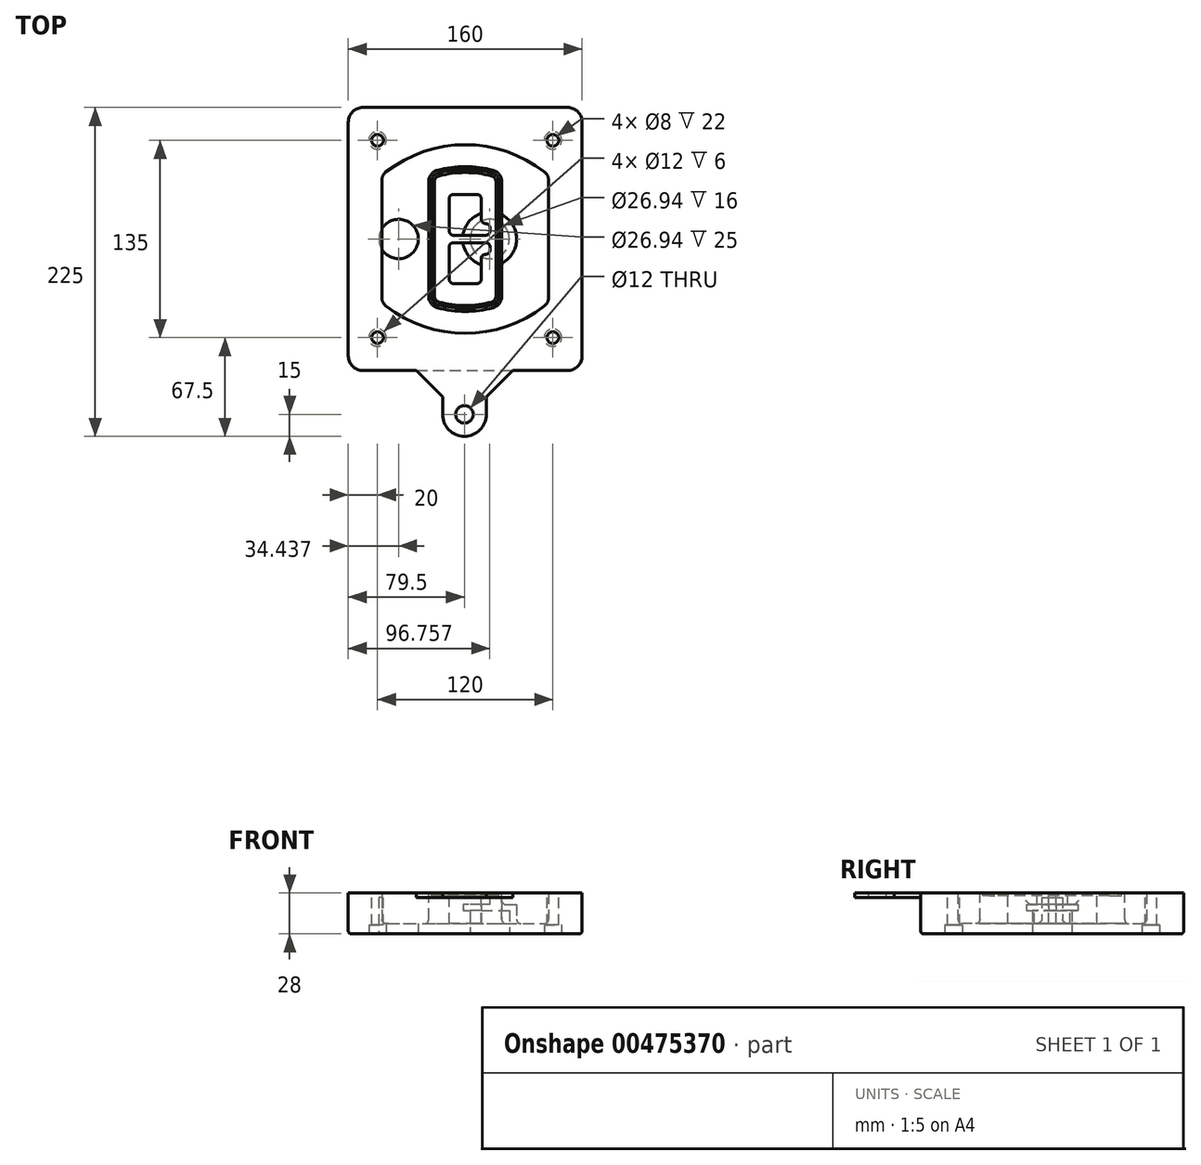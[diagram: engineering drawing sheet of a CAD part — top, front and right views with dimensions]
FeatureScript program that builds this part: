
annotation { "Feature Type Name" : "Feature", "Feature Type Description" : "" }
export const myFeature = defineFeature(function(context is Context, id is Id, definition is map)
    precondition{}
    {
        {
            var Q0;
            Q0=qCreatedBy(makeId("Top.planeOp"),FACE);
            var sketch = newSketch(context, id + "F0", { "sketchPlane" : qUnion([Q0])});
            skPoint(sketch, "E0.rect.middle", {"position": v(0, 0) * mm});
            skLineSegment(sketch, "E1.bottom", {"start": v(-70, -90) * mm, "end": v(70, -90) * mm});
            skLineSegment(sketch, "E1.top", {"start": v(-70, 90) * mm, "end": v(70, 90) * mm});
            skLineSegment(sketch, "E1.left", {"start": v(-80, -80) * mm, "end": v(-80, 80) * mm});
            skLineSegment(sketch, "E1.right", {"start": v(80, -80) * mm, "end": v(80, 80) * mm});
            skLineSegment(sketch, "E2", {"start": v(-80, 90) * mm, "end": v(80, -90) * mm, "construction": true});
            skLineSegment(sketch, "E3", {"start": v(80, 90) * mm, "end": v(-80, -90) * mm, "construction": true});
            skCircle(sketch, "E4", {"center": v(-60, 67.5) * mm, "radius": 4 * mm});
            skCircle(sketch, "E5", {"center": v(60, 67.5) * mm, "radius": 4 * mm});
            skCircle(sketch, "E6", {"center": v(60, -67.5) * mm, "radius": 4 * mm});
            skCircle(sketch, "E7", {"center": v(-60, -67.5) * mm, "radius": 4 * mm});
            skLineSegment(sketch, "E8", {"start": v(-60, 67.5) * mm, "end": v(60, 67.5) * mm, "construction": true});
            skLineSegment(sketch, "E9", {"start": v(60, 67.5) * mm, "end": v(60, -67.5) * mm, "construction": true});
            skLineSegment(sketch, "E10", {"start": v(60, -67.5) * mm, "end": v(-60, -67.5) * mm, "construction": true});
            skLineSegment(sketch, "E11", {"start": v(-60, -67.5) * mm, "end": v(-60, 67.5) * mm, "construction": true});
            skLineSegment(sketch, "E12", {"start": v(-60, 40.3) * mm, "end": v(-60, -40.3) * mm});
            skLineSegment(sketch, "E13", {"start": v(60, 40.3) * mm, "end": v(60, -40.3) * mm});
            skArc(sketch, "E14", {"start": v(56.15, 48.18) * mm, "mid": v(0, 67.5) * mm, "end": v(-56.15, 48.18) * mm});
            skArc(sketch, "E15", {"start": v(-56.15, -48.18) * mm, "mid": v(0, -67.5) * mm, "end": v(56.15, -48.18) * mm});
            skLineSegment(sketch, "E16", {"start": v(-60, 0) * mm, "end": v(60, 0) * mm, "construction": true});
            skPoint(sketch, "E17.visualSharp", {"position": v(-60, -45) * mm});
            skArc(sketch, "E17.filletArc", {"start": v(-60, -40.3) * mm, "mid": v(-58.99, -44.68) * mm, "end": v(-56.15, -48.18) * mm});
            skPoint(sketch, "E18.visualSharp", {"position": v(-60, 45) * mm});
            skArc(sketch, "E18.filletArc", {"start": v(-56.15, 48.18) * mm, "mid": v(-58.99, 44.68) * mm, "end": v(-60, 40.3) * mm});
            skPoint(sketch, "E19.visualSharp", {"position": v(60, 45) * mm});
            skArc(sketch, "E19.filletArc", {"start": v(60, 40.3) * mm, "mid": v(58.99, 44.68) * mm, "end": v(56.15, 48.18) * mm});
            skPoint(sketch, "E20.visualSharp", {"position": v(60, -45) * mm});
            skArc(sketch, "E20.filletArc", {"start": v(56.15, -48.18) * mm, "mid": v(58.99, -44.68) * mm, "end": v(60, -40.3) * mm});
            skPoint(sketch, "E21.visualSharp", {"position": v(-80, 90) * mm});
            skArc(sketch, "E21.filletArc", {"start": v(-70, 90) * mm, "mid": v(-77.07, 87.07) * mm, "end": v(-80, 80) * mm});
            skPoint(sketch, "E22.visualSharp", {"position": v(80, 90) * mm});
            skArc(sketch, "E22.filletArc", {"start": v(80, 80) * mm, "mid": v(77.07, 87.07) * mm, "end": v(70, 90) * mm});
            skPoint(sketch, "E23.visualSharp", {"position": v(80, -90) * mm});
            skArc(sketch, "E23.filletArc", {"start": v(70, -90) * mm, "mid": v(77.07, -87.07) * mm, "end": v(80, -80) * mm});
            skPoint(sketch, "E24.visualSharp", {"position": v(-80, -90) * mm});
            skArc(sketch, "E24.filletArc", {"start": v(-80, -80) * mm, "mid": v(-77.07, -87.07) * mm, "end": v(-70, -90) * mm});
            skArc(sketch, "E25.0", {"start": v(57, 40.3) * mm, "mid": v(56.3, 43.36) * mm, "end": v(54.3, 45.81) * mm});
            skLineSegment(sketch, "E25.1", {"start": v(57, 40.3) * mm, "end": v(57, -40.3) * mm});
            skArc(sketch, "E25.2", {"start": v(54.3, -45.81) * mm, "mid": v(56.3, -43.36) * mm, "end": v(57, -40.3) * mm});
            skArc(sketch, "E25.3", {"start": v(-54.3, -45.81) * mm, "mid": v(0, -64.5) * mm, "end": v(54.3, -45.81) * mm});
            skArc(sketch, "E25.4", {"start": v(-57, -40.3) * mm, "mid": v(-56.3, -43.36) * mm, "end": v(-54.3, -45.81) * mm});
            skArc(sketch, "E25.5", {"start": v(54.3, 45.81) * mm, "mid": v(0, 64.5) * mm, "end": v(-54.3, 45.81) * mm});
            skLineSegment(sketch, "E25.6", {"start": v(-57, 40.3) * mm, "end": v(-57, -40.3) * mm});
            skArc(sketch, "E25.7", {"start": v(-54.3, 45.81) * mm, "mid": v(-56.3, 43.36) * mm, "end": v(-57, 40.3) * mm});
            skArc(sketch, "E26.0", {"start": v(-58.62, 51.33) * mm, "mid": v(-62.58, 46.43) * mm, "end": v(-64, 40.3) * mm});
            skArc(sketch, "E26.1", {"start": v(58.62, 51.33) * mm, "mid": v(0, 71.5) * mm, "end": v(-58.62, 51.33) * mm});
            skArc(sketch, "E26.2", {"start": v(64, 40.3) * mm, "mid": v(62.58, 46.43) * mm, "end": v(58.62, 51.33) * mm});
            skLineSegment(sketch, "E26.3", {"start": v(64, 40.3) * mm, "end": v(64, -40.3) * mm});
            skArc(sketch, "E26.4", {"start": v(58.62, -51.33) * mm, "mid": v(62.58, -46.43) * mm, "end": v(64, -40.3) * mm});
            skLineSegment(sketch, "E26.5", {"start": v(-64, 40.3) * mm, "end": v(-64, -40.3) * mm});
            skArc(sketch, "E26.6", {"start": v(-58.62, -51.33) * mm, "mid": v(0, -71.5) * mm, "end": v(58.62, -51.33) * mm});
            skArc(sketch, "E26.7", {"start": v(-64, -40.3) * mm, "mid": v(-62.58, -46.43) * mm, "end": v(-58.62, -51.33) * mm});
            skSolve(sketch);
        }
        {
            var Q0;
            Q0=makeQuery(id+"F0.imprint","IMPRINT",FACE,{"disambiguationData":[TD([[makeQuery(id+"F0.imprint","IMPRINT",EDGE,{"derivedFrom":sQuery(id+"F0.wireOp",EDGE,"E1.bottom")}),1.0]])]});
            var Q1;
            Q1=makeQuery(id+"F0.imprint","IMPRINT",FACE,{"disambiguationData":[TD([[makeQuery(id+"F0.imprint","IMPRINT",EDGE,{"derivedFrom":sQuery(id+"F0.wireOp",EDGE,"E12")}),1.0]])]});
            var Q2;
            Q2=makeQuery(id+"F0.imprint","IMPRINT",FACE,{"disambiguationData":[TD([[makeQuery(id+"F0.imprint","IMPRINT",EDGE,{"derivedFrom":sQuery(id+"F0.wireOp",EDGE,"E25.0")}),1.0]])]});
            var Q3;
            Q3=makeQuery(id+"F0.imprint","IMPRINT",FACE,{"disambiguationData":[TD([[makeQuery(id+"F0.imprint","IMPRINT",EDGE,{"derivedFrom":sQuery(id+"F0.wireOp",EDGE,"E12")}),-1.0]])]});
            extrude(context, id + "F1", {"entities" : qUnion([Q0, Q1, Q2, Q3]), "oppositeDirection" : true, "depth" : 25 * mm});
        }
        {
            var Q0;
            Q0=makeQuery(id+"F0.imprint","IMPRINT",FACE,{"disambiguationData":[TD([[makeQuery(id+"F0.imprint","IMPRINT",EDGE,{"derivedFrom":sQuery(id+"F0.wireOp",EDGE,"E12")}),1.0]])]});
            extrude(context, id + "F2", {"entities" : qUnion([Q0]), "operationType" : NewBodyOperationType.ADD, "depth" : 3 * mm});
        }
        {
            var Q0;
            Q0=makeQuery(id+"F0.imprint","IMPRINT",FACE,{"disambiguationData":[TD([[makeQuery(id+"F0.imprint","IMPRINT",EDGE,{"derivedFrom":sQuery(id+"F0.wireOp",EDGE,"E25.0")}),1.0]])]});
            extrude(context, id + "F3", {"entities" : qUnion([Q0]), "operationType" : NewBodyOperationType.REMOVE, "oppositeDirection" : true, "depth" : 18 * mm});
        }
        {
            var Q0;
            Q0=makeQuery(id+"F2.opExtrude","CAP_FACE",FACE,{"disambiguationData":[OSD([sQuery(id+"F0.wireOp",EDGE,"E12"),sQuery(id+"F0.wireOp",EDGE,"E13"),sQuery(id+"F0.wireOp",EDGE,"E14"),sQuery(id+"F0.wireOp",EDGE,"E15"),sQuery(id+"F0.wireOp",EDGE,"E17.filletArc"),sQuery(id+"F0.wireOp",EDGE,"E18.filletArc"),sQuery(id+"F0.wireOp",EDGE,"E19.filletArc"),sQuery(id+"F0.wireOp",EDGE,"E20.filletArc"),sQuery(id+"F0.wireOp",EDGE,"E25.0"),sQuery(id+"F0.wireOp",EDGE,"E25.1"),sQuery(id+"F0.wireOp",EDGE,"E25.2"),sQuery(id+"F0.wireOp",EDGE,"E25.3"),sQuery(id+"F0.wireOp",EDGE,"E25.4"),sQuery(id+"F0.wireOp",EDGE,"E25.5"),sQuery(id+"F0.wireOp",EDGE,"E25.6"),sQuery(id+"F0.wireOp",EDGE,"E25.7")])],"isStart":false});
            var sketch = newSketch(context, id + "F4", { "sketchPlane" : qUnion([Q0])});
            skArc(sketch, "E27.0", {"start": v(-19.08, -46.97) * mm, "mid": v(0, -49.5) * mm, "end": v(19.08, -46.97) * mm});
            skArc(sketch, "E28.0", {"start": v(19.08, 46.97) * mm, "mid": v(0, 49.5) * mm, "end": v(-19.08, 46.97) * mm});
            skLineSegment(sketch, "E29", {"start": v(-25, 39.25) * mm, "end": v(-25, -39.25) * mm});
            skLineSegment(sketch, "E30", {"start": v(25, 39.25) * mm, "end": v(25, -39.25) * mm});
            skLineSegment(sketch, "E31", {"start": v(-25, 45.1) * mm, "end": v(25, 45.1) * mm, "construction": true});
            skLineSegment(sketch, "E32", {"start": v(-25, -45.1) * mm, "end": v(25, -45.1) * mm, "construction": true});
            skPoint(sketch, "E33.visualSharp", {"position": v(-25, 45.1) * mm});
            skArc(sketch, "E33.filletArc", {"start": v(-19.08, 46.97) * mm, "mid": v(-23.35, 44.11) * mm, "end": v(-25, 39.25) * mm});
            skPoint(sketch, "E34.visualSharp", {"position": v(25, 45.1) * mm});
            skArc(sketch, "E34.filletArc", {"start": v(25, 39.25) * mm, "mid": v(23.35, 44.11) * mm, "end": v(19.08, 46.97) * mm});
            skPoint(sketch, "E35.visualSharp", {"position": v(25, -45.1) * mm});
            skArc(sketch, "E35.filletArc", {"start": v(19.08, -46.97) * mm, "mid": v(23.35, -44.11) * mm, "end": v(25, -39.25) * mm});
            skPoint(sketch, "E36.visualSharp", {"position": v(-25, -45.1) * mm});
            skArc(sketch, "E36.filletArc", {"start": v(-25, -39.25) * mm, "mid": v(-23.35, -44.11) * mm, "end": v(-19.08, -46.97) * mm});
            skArc(sketch, "E37.0", {"start": v(54.3, 45.81) * mm, "mid": v(0, 64.5) * mm, "end": v(-54.3, 45.81) * mm});
            skArc(sketch, "E37.1", {"start": v(-54.3, 45.81) * mm, "mid": v(-56.3, 43.36) * mm, "end": v(-57, 40.3) * mm});
            skLineSegment(sketch, "E37.2", {"start": v(-57, 40.3) * mm, "end": v(-57, -40.3) * mm});
            skArc(sketch, "E37.3", {"start": v(-57, -40.3) * mm, "mid": v(-56.3, -43.36) * mm, "end": v(-54.3, -45.81) * mm});
            skArc(sketch, "E37.4", {"start": v(-54.3, -45.81) * mm, "mid": v(0, -64.5) * mm, "end": v(54.3, -45.81) * mm});
            skArc(sketch, "E37.5", {"start": v(54.3, -45.81) * mm, "mid": v(56.3, -43.36) * mm, "end": v(57, -40.3) * mm});
            skLineSegment(sketch, "E37.6", {"start": v(57, 40.3) * mm, "end": v(57, -40.3) * mm});
            skArc(sketch, "E37.7", {"start": v(57, 40.3) * mm, "mid": v(56.3, 43.36) * mm, "end": v(54.3, 45.81) * mm});
            skLineSegment(sketch, "E38.0", {"start": v(23, 39.25) * mm, "end": v(23, -39.25) * mm});
            skArc(sketch, "E38.1", {"start": v(18.56, -45.04) * mm, "mid": v(21.76, -42.9) * mm, "end": v(23, -39.25) * mm});
            skArc(sketch, "E38.2", {"start": v(-18.56, -45.04) * mm, "mid": v(0, -47.5) * mm, "end": v(18.56, -45.04) * mm});
            skArc(sketch, "E38.3", {"start": v(-23, -39.25) * mm, "mid": v(-21.76, -42.9) * mm, "end": v(-18.56, -45.04) * mm});
            skLineSegment(sketch, "E38.4", {"start": v(-23, 39.25) * mm, "end": v(-23, -39.25) * mm});
            skArc(sketch, "E38.5", {"start": v(23, 39.25) * mm, "mid": v(21.76, 42.9) * mm, "end": v(18.56, 45.04) * mm});
            skArc(sketch, "E38.6", {"start": v(-18.56, 45.04) * mm, "mid": v(-21.76, 42.9) * mm, "end": v(-23, 39.25) * mm});
            skArc(sketch, "E38.7", {"start": v(18.56, 45.04) * mm, "mid": v(0, 47.5) * mm, "end": v(-18.56, 45.04) * mm});
            skArc(sketch, "E39.0", {"start": v(21, 39.25) * mm, "mid": v(20.18, 41.68) * mm, "end": v(18.04, 43.1) * mm});
            skLineSegment(sketch, "E39.1", {"start": v(21, 39.25) * mm, "end": v(21, -39.25) * mm});
            skArc(sketch, "E39.2", {"start": v(18.04, -43.1) * mm, "mid": v(20.18, -41.68) * mm, "end": v(21, -39.25) * mm});
            skArc(sketch, "E39.3", {"start": v(-18.04, -43.1) * mm, "mid": v(0, -45.5) * mm, "end": v(18.04, -43.1) * mm});
            skArc(sketch, "E39.4", {"start": v(-21, -39.25) * mm, "mid": v(-20.18, -41.68) * mm, "end": v(-18.04, -43.1) * mm});
            skArc(sketch, "E39.5", {"start": v(18.04, 43.1) * mm, "mid": v(0, 45.5) * mm, "end": v(-18.04, 43.1) * mm});
            skLineSegment(sketch, "E39.6", {"start": v(-21, 39.25) * mm, "end": v(-21, -39.25) * mm});
            skArc(sketch, "E39.7", {"start": v(-18.04, 43.1) * mm, "mid": v(-20.18, 41.68) * mm, "end": v(-21, 39.25) * mm});
            skLineSegment(sketch, "E40", {"start": v(-25, 0) * mm, "end": v(25, 0) * mm, "construction": true});
            skLineSegment(sketch, "E41", {"start": v(-11, 5.5) * mm, "end": v(-11, 27.5) * mm});
            skLineSegment(sketch, "E42", {"start": v(-8, 30.5) * mm, "end": v(8, 30.5) * mm});
            skLineSegment(sketch, "E43", {"start": v(11, 27.5) * mm, "end": v(11, 13.5) * mm});
            skLineSegment(sketch, "E44", {"start": v(14, 10.5) * mm, "end": v(14, 10.5) * mm});
            skLineSegment(sketch, "E45", {"start": v(17, 7.5) * mm, "end": v(17, 5.5) * mm});
            skLineSegment(sketch, "E46", {"start": v(14, 2.5) * mm, "end": v(-8, 2.5) * mm});
            skPoint(sketch, "E47.visualSharp", {"position": v(-11, 30.5) * mm});
            skArc(sketch, "E47.filletArc", {"start": v(-8, 30.5) * mm, "mid": v(-10.12, 29.62) * mm, "end": v(-11, 27.5) * mm});
            skPoint(sketch, "E48.visualSharp", {"position": v(11, 30.5) * mm});
            skArc(sketch, "E48.filletArc", {"start": v(11, 27.5) * mm, "mid": v(10.12, 29.62) * mm, "end": v(8, 30.5) * mm});
            skPoint(sketch, "E49.visualSharp", {"position": v(11, 10.5) * mm});
            skArc(sketch, "E49.filletArc", {"start": v(11, 13.5) * mm, "mid": v(11.88, 11.38) * mm, "end": v(14, 10.5) * mm});
            skPoint(sketch, "E50.visualSharp", {"position": v(17, 10.5) * mm});
            skArc(sketch, "E50.filletArc", {"start": v(17, 7.5) * mm, "mid": v(16.12, 9.62) * mm, "end": v(14, 10.5) * mm});
            skPoint(sketch, "E51.visualSharp", {"position": v(17, 2.5) * mm});
            skArc(sketch, "E51.filletArc", {"start": v(14, 2.5) * mm, "mid": v(16.12, 3.38) * mm, "end": v(17, 5.5) * mm});
            skPoint(sketch, "E52.visualSharp", {"position": v(-11, 2.5) * mm});
            skArc(sketch, "E52.filletArc", {"start": v(-11, 5.5) * mm, "mid": v(-10.12, 3.38) * mm, "end": v(-8, 2.5) * mm});
            skLineSegment(sketch, "E53.0.MirrorCS", {"start": v(14, -2.5) * mm, "end": v(-8, -2.5) * mm});
            skArc(sketch, "E54.0.MirrorCS", {"start": v(-11, -5.5) * mm, "mid": v(-10.12, -3.38) * mm, "end": v(-8, -2.5) * mm});
            skLineSegment(sketch, "E55.0.MirrorCS", {"start": v(-11, -5.5) * mm, "end": v(-11, -27.5) * mm});
            skArc(sketch, "E56.0.MirrorCS", {"start": v(-8, -30.5) * mm, "mid": v(-10.12, -29.62) * mm, "end": v(-11, -27.5) * mm});
            skLineSegment(sketch, "E57.0.MirrorCS", {"start": v(-8, -30.5) * mm, "end": v(8, -30.5) * mm});
            skArc(sketch, "E58.0.MirrorCS", {"start": v(11, -27.5) * mm, "mid": v(10.12, -29.62) * mm, "end": v(8, -30.5) * mm});
            skLineSegment(sketch, "E59.0.MirrorCS", {"start": v(11, -27.5) * mm, "end": v(11, -13.5) * mm});
            skArc(sketch, "E60.0.MirrorCS", {"start": v(11, -13.5) * mm, "mid": v(11.88, -11.38) * mm, "end": v(14, -10.5) * mm});
            skArc(sketch, "E61.0.MirrorCS", {"start": v(17, -7.5) * mm, "mid": v(16.12, -9.62) * mm, "end": v(14, -10.5) * mm});
            skLineSegment(sketch, "E62.0.MirrorCS", {"start": v(17, -7.5) * mm, "end": v(17, -5.5) * mm});
            skArc(sketch, "E63.0.MirrorCS", {"start": v(14, -2.5) * mm, "mid": v(16.12, -3.38) * mm, "end": v(17, -5.5) * mm});
            skSolve(sketch);
        }
        {
            var Q0;
            Q0=makeQuery(id+"F4.imprint","IMPRINT",FACE,{"disambiguationData":[TD([[makeQuery(id+"F4.imprint","IMPRINT",EDGE,{"derivedFrom":sQuery(id+"F4.wireOp",EDGE,"E27.0")}),1.0]])]});
            var Q1;
            Q1=makeQuery(id+"F4.imprint","IMPRINT",FACE,{"disambiguationData":[TD([[makeQuery(id+"F4.imprint","IMPRINT",EDGE,{"derivedFrom":sQuery(id+"F4.wireOp",EDGE,"E38.0")}),-1.0]])]});
            var Q2;
            Q2=makeQuery(id+"F4.imprint","IMPRINT",FACE,{"disambiguationData":[TD([[makeQuery(id+"F4.imprint","IMPRINT",EDGE,{"derivedFrom":sQuery(id+"F4.wireOp",EDGE,"E39.0")}),1.0]])]});
            extrude(context, id + "F5", {"entities" : qUnion([Q0, Q1, Q2]), "operationType" : NewBodyOperationType.ADD, "endBound" : BoundingType.UP_TO_NEXT, "oppositeDirection" : true, "depth" : 25 * mm});
        }
        {
            var Q0;
            Q0=makeQuery(id+"F4.imprint","IMPRINT",FACE,{"disambiguationData":[TD([[makeQuery(id+"F4.imprint","IMPRINT",EDGE,{"derivedFrom":sQuery(id+"F4.wireOp",EDGE,"E38.0")}),-1.0]])]});
            extrude(context, id + "F6", {"entities" : qUnion([Q0]), "operationType" : NewBodyOperationType.REMOVE, "oppositeDirection" : true, "depth" : 2 * mm});
        }
        {
            var Q0;
            Q0=makeQuery(id+"F1.opExtrude","CAP_FACE",FACE,{"disambiguationData":[OSD([sQuery(id+"F0.wireOp",EDGE,"E1.bottom"),sQuery(id+"F0.wireOp",EDGE,"E1.top"),sQuery(id+"F0.wireOp",EDGE,"E1.left"),sQuery(id+"F0.wireOp",EDGE,"E1.right"),sQuery(id+"F0.wireOp",EDGE,"E4"),sQuery(id+"F0.wireOp",EDGE,"E5"),sQuery(id+"F0.wireOp",EDGE,"E6"),sQuery(id+"F0.wireOp",EDGE,"E7"),sQuery(id+"F0.wireOp",EDGE,"E21.filletArc"),sQuery(id+"F0.wireOp",EDGE,"E22.filletArc"),sQuery(id+"F0.wireOp",EDGE,"E23.filletArc"),sQuery(id+"F0.wireOp",EDGE,"E24.filletArc")])],"isStart":false});
            var sketch = newSketch(context, id + "F7", { "sketchPlane" : qUnion([Q0])});
            skCircle(sketch, "E64", {"center": v(16.76, 0) * mm, "radius": 13.47 * mm});
            skCircle(sketch, "E65", {"center": v(-45.56, 0) * mm, "radius": 13.47 * mm});
            skLineSegment(sketch, "E66", {"start": v(80, 0) * mm, "end": v(-80, 0) * mm});
            skCircle(sketch, "E67", {"center": v(16.76, 0) * mm, "radius": 18.47 * mm});
            skCircle(sketch, "E68", {"center": v(60, -67.5) * mm, "radius": 6 * mm});
            skCircle(sketch, "E69", {"center": v(-60, -67.5) * mm, "radius": 6 * mm});
            skCircle(sketch, "E70", {"center": v(-60, 67.5) * mm, "radius": 6 * mm});
            skCircle(sketch, "E71", {"center": v(60, 67.5) * mm, "radius": 6 * mm});
            skSolve(sketch);
        }
        {
            var Q0;
            {var subQ1=sQuery(id+"F7.wireOp",EDGE,"E66");var subQ4=sQuery(id+"F7.wireOp",EDGE,"E64");var subQ6=makeQuery(id+"F7.imprint","INTERSECT",VERTEX,{"disambiguationData":[OD(0.0)],"derivedFrom":[subQ4,subQ1]});Q0=makeQuery(id+"F7.imprint","IMPRINT",FACE,{"disambiguationData":[TD([[makeQuery(id+"F7.imprint","IMPRINT",EDGE,{"disambiguationData":[TD([[subQ6,-1.0]])],"derivedFrom":subQ4}),-1.0]])]});}
            var Q1;
            {var subQ0=sQuery(id+"F7.wireOp",EDGE,"E66");var subQ1=sQuery(id+"F7.wireOp",EDGE,"E64");var subQ3=makeQuery(id+"F7.imprint","INTERSECT",VERTEX,{"disambiguationData":[OD(0.0)],"derivedFrom":[subQ1,subQ0]});Q1=makeQuery(id+"F7.imprint","IMPRINT",FACE,{"disambiguationData":[TD([[makeQuery(id+"F7.imprint","IMPRINT",EDGE,{"disambiguationData":[TD([[subQ3,-1.0]])],"derivedFrom":subQ1}),1.0]])]});}
            var Q2;
            {var subQ0=sQuery(id+"F7.wireOp",EDGE,"E66");var subQ1=sQuery(id+"F7.wireOp",EDGE,"E64");var subQ3=makeQuery(id+"F7.imprint","INTERSECT",VERTEX,{"disambiguationData":[OD(0.0)],"derivedFrom":[subQ1,subQ0]});Q2=makeQuery(id+"F7.imprint","IMPRINT",FACE,{"disambiguationData":[TD([[makeQuery(id+"F7.imprint","IMPRINT",EDGE,{"disambiguationData":[TD([[subQ3,1.0]])],"derivedFrom":subQ1}),1.0]])]});}
            var Q3;
            {var subQ1=sQuery(id+"F7.wireOp",EDGE,"E66");var subQ4=sQuery(id+"F7.wireOp",EDGE,"E64");var subQ6=makeQuery(id+"F7.imprint","INTERSECT",VERTEX,{"disambiguationData":[OD(0.0)],"derivedFrom":[subQ4,subQ1]});Q3=makeQuery(id+"F7.imprint","IMPRINT",FACE,{"disambiguationData":[TD([[makeQuery(id+"F7.imprint","IMPRINT",EDGE,{"disambiguationData":[TD([[subQ6,1.0]])],"derivedFrom":subQ4}),-1.0]])]});}
            extrude(context, id + "F8", {"entities" : qUnion([Q0, Q1, Q2, Q3]), "operationType" : NewBodyOperationType.ADD, "oppositeDirection" : true, "depth" : 20 * mm});
        }
        {
            var Q0;
            {var subQ0=sQuery(id+"F7.wireOp",EDGE,"E66");var subQ1=sQuery(id+"F7.wireOp",EDGE,"E64");var subQ3=makeQuery(id+"F7.imprint","INTERSECT",VERTEX,{"disambiguationData":[OD(0.0)],"derivedFrom":[subQ1,subQ0]});Q0=makeQuery(id+"F7.imprint","IMPRINT",FACE,{"disambiguationData":[TD([[makeQuery(id+"F7.imprint","IMPRINT",EDGE,{"disambiguationData":[TD([[subQ3,-1.0]])],"derivedFrom":subQ1}),1.0]])]});}
            var Q1;
            {var subQ0=sQuery(id+"F7.wireOp",EDGE,"E66");var subQ1=sQuery(id+"F7.wireOp",EDGE,"E64");var subQ3=makeQuery(id+"F7.imprint","INTERSECT",VERTEX,{"disambiguationData":[OD(0.0)],"derivedFrom":[subQ1,subQ0]});Q1=makeQuery(id+"F7.imprint","IMPRINT",FACE,{"disambiguationData":[TD([[makeQuery(id+"F7.imprint","IMPRINT",EDGE,{"disambiguationData":[TD([[subQ3,1.0]])],"derivedFrom":subQ1}),1.0]])]});}
            extrude(context, id + "F9", {"entities" : qUnion([Q0, Q1]), "operationType" : NewBodyOperationType.REMOVE, "oppositeDirection" : true, "depth" : 16 * mm});
        }
        {
            var Q0;
            {var subQ0=sQuery(id+"F7.wireOp",EDGE,"E66");var subQ1=sQuery(id+"F7.wireOp",EDGE,"E65");var subQ3=makeQuery(id+"F7.imprint","INTERSECT",VERTEX,{"disambiguationData":[OD(0.0)],"derivedFrom":[subQ1,subQ0]});Q0=makeQuery(id+"F7.imprint","IMPRINT",FACE,{"disambiguationData":[TD([[makeQuery(id+"F7.imprint","IMPRINT",EDGE,{"disambiguationData":[TD([[subQ3,-1.0]])],"derivedFrom":subQ1}),1.0]])]});}
            var Q1;
            {var subQ0=sQuery(id+"F7.wireOp",EDGE,"E66");var subQ1=sQuery(id+"F7.wireOp",EDGE,"E65");var subQ3=makeQuery(id+"F7.imprint","INTERSECT",VERTEX,{"disambiguationData":[OD(0.0)],"derivedFrom":[subQ1,subQ0]});Q1=makeQuery(id+"F7.imprint","IMPRINT",FACE,{"disambiguationData":[TD([[makeQuery(id+"F7.imprint","IMPRINT",EDGE,{"disambiguationData":[TD([[subQ3,1.0]])],"derivedFrom":subQ1}),1.0]])]});}
            extrude(context, id + "F10", {"entities" : qUnion([Q0, Q1]), "operationType" : NewBodyOperationType.REMOVE, "oppositeDirection" : true, "depth" : 25 * mm});
        }
        {
            var Q0;
            Q0=makeQuery(id+"F7.imprint","IMPRINT",FACE,{"disambiguationData":[TD([[makeQuery(id+"F7.imprint","IMPRINT",EDGE,{"derivedFrom":sQuery(id+"F7.wireOp",EDGE,"E68")}),1.0]])]});
            var Q1;
            Q1=makeQuery(id+"F7.imprint","IMPRINT",FACE,{"disambiguationData":[TD([[makeQuery(id+"F7.imprint","IMPRINT",EDGE,{"derivedFrom":makeQuery(id+"F1.opExtrude","CAP_EDGE",EDGE,{"disambiguationData":[OSD([sQuery(id+"F0.wireOp",EDGE,"E5")])],"isStart":false})}),-1.0]])]});
            var Q2;
            Q2=makeQuery(id+"F7.imprint","IMPRINT",FACE,{"disambiguationData":[TD([[makeQuery(id+"F7.imprint","IMPRINT",EDGE,{"derivedFrom":sQuery(id+"F7.wireOp",EDGE,"E69")}),1.0]])]});
            var Q3;
            Q3=makeQuery(id+"F7.imprint","IMPRINT",FACE,{"disambiguationData":[TD([[makeQuery(id+"F7.imprint","IMPRINT",EDGE,{"derivedFrom":makeQuery(id+"F1.opExtrude","CAP_EDGE",EDGE,{"disambiguationData":[OSD([sQuery(id+"F0.wireOp",EDGE,"E4")])],"isStart":false})}),-1.0]])]});
            var Q4;
            Q4=makeQuery(id+"F7.imprint","IMPRINT",FACE,{"disambiguationData":[TD([[makeQuery(id+"F7.imprint","IMPRINT",EDGE,{"derivedFrom":sQuery(id+"F7.wireOp",EDGE,"E70")}),1.0]])]});
            var Q5;
            Q5=makeQuery(id+"F7.imprint","IMPRINT",FACE,{"disambiguationData":[TD([[makeQuery(id+"F7.imprint","IMPRINT",EDGE,{"derivedFrom":makeQuery(id+"F1.opExtrude","CAP_EDGE",EDGE,{"disambiguationData":[OSD([sQuery(id+"F0.wireOp",EDGE,"E7")])],"isStart":false})}),-1.0]])]});
            var Q6;
            Q6=makeQuery(id+"F7.imprint","IMPRINT",FACE,{"disambiguationData":[TD([[makeQuery(id+"F7.imprint","IMPRINT",EDGE,{"derivedFrom":sQuery(id+"F7.wireOp",EDGE,"E71")}),1.0]])]});
            var Q7;
            Q7=makeQuery(id+"F7.imprint","IMPRINT",FACE,{"disambiguationData":[TD([[makeQuery(id+"F7.imprint","IMPRINT",EDGE,{"derivedFrom":makeQuery(id+"F1.opExtrude","CAP_EDGE",EDGE,{"disambiguationData":[OSD([sQuery(id+"F0.wireOp",EDGE,"E6")])],"isStart":false})}),-1.0]])]});
            extrude(context, id + "F11", {"entities" : qUnion([Q0, Q1, Q2, Q3, Q4, Q5, Q6, Q7]), "operationType" : NewBodyOperationType.REMOVE, "oppositeDirection" : true, "depth" : 6 * mm});
        }
        {
            var Q0;
            Q0=makeQuery(id+"F9.boolean.opBoolean","COPY",FACE,{"derivedFrom":makeQuery(id+"F9.opExtrude","CAP_FACE",FACE,{"disambiguationData":[OSD([sQuery(id+"F7.wireOp",EDGE,"E64")])],"isStart":false})});
            var sketch = newSketch(context, id + "F12", { "sketchPlane" : qUnion([Q0])});
            skArc(sketch, "E72.0", {"start": v(11, 17.55) * mm, "mid": v(2.57, 11.82) * mm, "end": v(-1.54, 2.5) * mm});
            skArc(sketch, "E72.1", {"start": v(-1.54, -2.5) * mm, "mid": v(2.57, -11.82) * mm, "end": v(11, -17.55) * mm});
            skLineSegment(sketch, "E73", {"start": v(-1.54, -2.5) * mm, "end": v(14, -2.5) * mm});
            skLineSegment(sketch, "E74.0", {"start": v(14, 2.5) * mm, "end": v(-1.54, 2.5) * mm});
            skArc(sketch, "E74.1", {"start": v(14, 2.5) * mm, "mid": v(16.12, 3.38) * mm, "end": v(17, 5.5) * mm});
            skLineSegment(sketch, "E74.2", {"start": v(17, 7.5) * mm, "end": v(17, 5.5) * mm});
            skArc(sketch, "E74.3", {"start": v(17, 7.5) * mm, "mid": v(16.12, 9.62) * mm, "end": v(14, 10.5) * mm});
            skArc(sketch, "E74.4", {"start": v(11, 13.5) * mm, "mid": v(11.88, 11.38) * mm, "end": v(14, 10.5) * mm});
            skLineSegment(sketch, "E74.5", {"start": v(11, 17.55) * mm, "end": v(11, 13.5) * mm});
            skLineSegment(sketch, "E74.7", {"start": v(14, -2.5) * mm, "end": v(-1.54, -2.5) * mm});
            skArc(sketch, "E74.8", {"start": v(14, -2.5) * mm, "mid": v(16.12, -3.38) * mm, "end": v(17, -5.5) * mm});
            skLineSegment(sketch, "E74.9", {"start": v(17, -7.5) * mm, "end": v(17, -5.5) * mm});
            skArc(sketch, "E74.10", {"start": v(17, -7.5) * mm, "mid": v(16.12, -9.62) * mm, "end": v(14, -10.5) * mm});
            skArc(sketch, "E74.11", {"start": v(11, -13.5) * mm, "mid": v(11.88, -11.38) * mm, "end": v(14, -10.5) * mm});
            skLineSegment(sketch, "E74.12", {"start": v(11, -17.55) * mm, "end": v(11, -13.5) * mm});
            skPoint(sketch, "E75.orphan", {"position": v(11, -27.5) * mm});
            skPoint(sketch, "E76.orphan", {"position": v(-8, -2.5) * mm});
            skPoint(sketch, "E77.orphan", {"position": v(-8, 2.5) * mm});
            skPoint(sketch, "E78.orphan", {"position": v(11, 27.5) * mm});
            skSolve(sketch);
        }
        {
            var Q0;
            {var subQ7=sQuery(id+"F12.wireOp",EDGE,"E72.0");var subQ14=sQuery(id+"F12.wireOp",EDGE,"E72.1");var subQ16=sQuery(id+"F12.wireOp",EDGE,"E74.1");var subQ18=sQuery(id+"F12.wireOp",EDGE,"E74.8");Q0=qUnion([makeQuery(id+"F12.imprint","IMPRINT",FACE,{"disambiguationData":[TD([[makeQuery(id+"F12.imprint","IMPRINT",EDGE,{"derivedFrom":subQ7}),1.0]])]}),makeQuery(id+"F12.imprint","IMPRINT",FACE,{"disambiguationData":[TD([[makeQuery(id+"F12.imprint","IMPRINT",EDGE,{"derivedFrom":subQ14}),1.0]])]}),makeQuery(id+"F12.imprint","IMPRINT",FACE,{"disambiguationData":[TD([[makeQuery(id+"F12.imprint","IMPRINT",EDGE,{"derivedFrom":subQ16}),1.0]])]}),makeQuery(id+"F12.imprint","IMPRINT",FACE,{"disambiguationData":[TD([[makeQuery(id+"F12.imprint","IMPRINT",EDGE,{"derivedFrom":subQ18}),-1.0]])]})]);}
            var Q1;
            Q1=makeQuery(id+"F5.boolean.opBoolean","SPLIT",FACE,{"disambiguationData":[TD([makeQuery(id+"F5.opExtrude","SWEPT_FACE",FACE,{"disambiguationData":[OSD([sQuery(id+"F4.wireOp",EDGE,"E41")])]})])],"derivedFrom":makeQuery(id+"F3.boolean.opBoolean","COPY",FACE,{"derivedFrom":makeQuery(id+"F3.opExtrude","CAP_FACE",FACE,{"disambiguationData":[OSD([sQuery(id+"F0.wireOp",EDGE,"E25.0"),sQuery(id+"F0.wireOp",EDGE,"E25.1"),sQuery(id+"F0.wireOp",EDGE,"E25.2"),sQuery(id+"F0.wireOp",EDGE,"E25.3"),sQuery(id+"F0.wireOp",EDGE,"E25.4"),sQuery(id+"F0.wireOp",EDGE,"E25.5"),sQuery(id+"F0.wireOp",EDGE,"E25.6"),sQuery(id+"F0.wireOp",EDGE,"E25.7")])],"isStart":false})})});
            extrude(context, id + "F13", {"entities" : qUnion([Q0]), "operationType" : NewBodyOperationType.REMOVE, "endBound" : BoundingType.UP_TO_SURFACE, "endBoundEntityFace" : qUnion([Q1]), "depth" : 25 * mm});
        }
        {
            var Q0;
            Q0=makeQuery(id+"F3.boolean.opBoolean","COPY",EDGE,{"derivedFrom":makeQuery(id+"F3.opExtrude","CAP_EDGE",EDGE,{"disambiguationData":[OSD([sQuery(id+"F0.wireOp",EDGE,"E25.6")])],"isStart":false})});
            var Q1;
            Q1=makeQuery(id+"F8.boolean.opBoolean","INTERSECT",EDGE,{"derivedFrom":[makeQuery(id+"F5.opExtrude","SWEPT_FACE",FACE,{"disambiguationData":[OSD([sQuery(id+"F4.wireOp",EDGE,"E30")])]}),makeQuery(id+"F8.opExtrude","CAP_FACE",FACE,{"disambiguationData":[OSD([sQuery(id+"F7.wireOp",EDGE,"E67")])],"isStart":false})]});
            var Q2;
            Q2=makeQuery(id+"F8.boolean.opBoolean","INTERSECT",EDGE,{"disambiguationData":[OD(1.0)],"derivedFrom":[makeQuery(id+"F5.opExtrude","SWEPT_FACE",FACE,{"disambiguationData":[OSD([sQuery(id+"F4.wireOp",EDGE,"E30")])]}),makeQuery(id+"F8.opExtrude","SWEPT_FACE",FACE,{"disambiguationData":[OSD([sQuery(id+"F7.wireOp",EDGE,"E67")])]})]});
            var Q3;
            {var subQ0=sQuery(id+"F4.wireOp",EDGE,"E30");Q3=makeQuery(id+"F8.boolean.opBoolean","SPLIT",EDGE,{"disambiguationData":[TD([makeQuery(id+"F5.opExtrude","SWEPT_FACE",FACE,{"disambiguationData":[OSD([sQuery(id+"F4.wireOp",EDGE,"E35.filletArc")])]})])],"derivedFrom":makeQuery(id+"F5.opExtrude","CAP_EDGE",EDGE,{"disambiguationData":[OSD([subQ0])],"isStart":false})});}
            var Q4;
            {var subQ0=sQuery(id+"F0.wireOp",EDGE,"E25.7");var subQ1=sQuery(id+"F0.wireOp",EDGE,"E25.1");var subQ2=sQuery(id+"F0.wireOp",EDGE,"E25.6");var subQ3=sQuery(id+"F0.wireOp",EDGE,"E25.5");var subQ4=sQuery(id+"F0.wireOp",EDGE,"E25.4");var subQ5=sQuery(id+"F0.wireOp",EDGE,"E25.0");var subQ6=sQuery(id+"F0.wireOp",EDGE,"E25.2");var subQ7=sQuery(id+"F0.wireOp",EDGE,"E25.3");Q4=makeQuery(id+"F8.boolean.opBoolean","INTERSECT",EDGE,{"derivedFrom":[makeQuery(id+"F5.boolean.opBoolean","SPLIT",FACE,{"disambiguationData":[TD([makeQuery(id+"F2.opExtrude","SWEPT_FACE",FACE,{"disambiguationData":[OSD([subQ5])]})])],"derivedFrom":makeQuery(id+"F3.boolean.opBoolean","COPY",FACE,{"derivedFrom":makeQuery(id+"F3.opExtrude","CAP_FACE",FACE,{"disambiguationData":[OSD([subQ5,subQ1,subQ6,subQ7,subQ4,subQ3,subQ2,subQ0])],"isStart":false})})}),makeQuery(id+"F8.opExtrude","SWEPT_FACE",FACE,{"disambiguationData":[OSD([sQuery(id+"F7.wireOp",EDGE,"E67")])]})]});}
            var Q5;
            Q5=makeQuery(id+"F8.boolean.opBoolean","INTERSECT",EDGE,{"disambiguationData":[OD(0.0)],"derivedFrom":[makeQuery(id+"F5.opExtrude","SWEPT_FACE",FACE,{"disambiguationData":[OSD([sQuery(id+"F4.wireOp",EDGE,"E30")])]}),makeQuery(id+"F8.opExtrude","SWEPT_FACE",FACE,{"disambiguationData":[OSD([sQuery(id+"F7.wireOp",EDGE,"E67")])]})]});
            fillet(context, id + "F14", {"entities" : qUnion([Q0, Q1, Q2, Q3, Q4, Q5]), "radius" : 3 * mm, "tangentPropagation" : true, "allowEdgeOverflow" : false});
        }
        {
            var Q0;
            Q0=makeQuery(id+"F1.opExtrude","CAP_EDGE",EDGE,{"disambiguationData":[OSD([sQuery(id+"F0.wireOp",EDGE,"E1.bottom")])],"isStart":false});
            fillet(context, id + "F15", {"entities" : qUnion([Q0]), "radius" : 2 * mm, "tangentPropagation" : true, "allowEdgeOverflow" : false});
        }
        {
            var Q0;
            {var subQ0=sQuery(id+"F0.wireOp",EDGE,"E21.filletArc");var subQ1=sQuery(id+"F0.wireOp",EDGE,"E7");var subQ2=sQuery(id+"F0.wireOp",EDGE,"E6");var subQ3=sQuery(id+"F0.wireOp",EDGE,"E5");var subQ4=sQuery(id+"F0.wireOp",EDGE,"E4");var subQ5=sQuery(id+"F0.wireOp",EDGE,"E22.filletArc");var subQ6=sQuery(id+"F0.wireOp",EDGE,"E1.bottom");var subQ7=sQuery(id+"F0.wireOp",EDGE,"E1.right");var subQ8=sQuery(id+"F0.wireOp",EDGE,"E1.top");var subQ9=sQuery(id+"F0.wireOp",EDGE,"E1.left");var subQ10=sQuery(id+"F0.wireOp",EDGE,"E23.filletArc");var subQ11=sQuery(id+"F0.wireOp",EDGE,"E24.filletArc");Q0=makeQuery(id+"F2.boolean.opBoolean","SPLIT",FACE,{"disambiguationData":[TD([makeQuery(id+"F1.opExtrude","SWEPT_FACE",FACE,{"disambiguationData":[OSD([subQ6])]})])],"derivedFrom":makeQuery(id+"F1.opExtrude","CAP_FACE",FACE,{"disambiguationData":[OSD([subQ6,subQ8,subQ9,subQ7,subQ4,subQ3,subQ2,subQ1,subQ0,subQ5,subQ10,subQ11])],"isStart":true})});}
            var sketch = newSketch(context, id + "F16", { "sketchPlane" : qUnion([Q0])});
            skSolve(sketch);
        }
        {
            var Q0;
            Q0=makeQuery(id+"F16.imprint","IMPRINT",FACE,{"disambiguationData":[TD([[makeQuery(id+"F16.imprint","IMPRINT",EDGE,{"derivedFrom":makeQuery(id+"F1.opExtrude","CAP_EDGE",EDGE,{"disambiguationData":[OSD([sQuery(id+"F0.wireOp",EDGE,"E1.bottom")])],"isStart":true})}),1.0]])]});
            var sketch = newSketch(context, id + "F17", { "sketchPlane" : qUnion([Q0])});
            skLineSegment(sketch, "E79.0", {"start": v(-70, 90) * mm, "end": v(70, 90) * mm});
            skLineSegment(sketch, "E80.0.0", {"start": v(70, 90) * mm, "end": v(-70, 90) * mm});
            skArc(sketch, "E80.0.1", {"start": v(-70, 90) * mm, "mid": v(-77.07, 87.07) * mm, "end": v(-80, 80) * mm});
            skLineSegment(sketch, "E80.0.2", {"start": v(-80, 80) * mm, "end": v(-80, -80) * mm});
            skArc(sketch, "E80.0.3", {"start": v(-80, -80) * mm, "mid": v(-77.07, -87.07) * mm, "end": v(-70, -90) * mm});
            skLineSegment(sketch, "E80.0.4", {"start": v(-70, -90) * mm, "end": v(70, -90) * mm});
            skArc(sketch, "E80.0.5", {"start": v(70, -90) * mm, "mid": v(77.07, -87.07) * mm, "end": v(80, -80) * mm});
            skLineSegment(sketch, "E80.0.6", {"start": v(80, -80) * mm, "end": v(80, 80) * mm});
            skArc(sketch, "E80.0.7", {"start": v(80, 80) * mm, "mid": v(77.07, 87.07) * mm, "end": v(70, 90) * mm});
            skLineSegment(sketch, "E81", {"start": v(-33.5, 90) * mm, "end": v(-15.5, 108) * mm});
            skLineSegment(sketch, "E82", {"start": v(-15.5, 108) * mm, "end": v(-15.5, 120) * mm});
            skLineSegment(sketch, "E83", {"start": v(32.5, 90) * mm, "end": v(14.5, 108) * mm});
            skLineSegment(sketch, "E84", {"start": v(14.5, 108) * mm, "end": v(14.5, 120) * mm});
            skArc(sketch, "E85", {"start": v(14.5, 120) * mm, "mid": v(-0.5, 135) * mm, "end": v(-15.5, 120) * mm});
            skCircle(sketch, "E86", {"center": v(-0.5, 120) * mm, "radius": 6 * mm});
            skLineSegment(sketch, "E87", {"start": v(-0.5, 120) * mm, "end": v(-0.5, 90) * mm, "construction": true});
            skLineSegment(sketch, "E88", {"start": v(-80, 0) * mm, "end": v(80, 0) * mm, "construction": true});
            skArc(sketch, "E89.MirrorCS", {"start": v(-15.5, 120) * mm, "mid": v(-0.5, 135) * mm, "end": v(14.5, 120) * mm});
            skLineSegment(sketch, "E90.MirrorCS", {"start": v(32.5, -90) * mm, "end": v(14.5, -108) * mm});
            skLineSegment(sketch, "E91.MirrorCS", {"start": v(14.5, -108) * mm, "end": v(14.5, -120) * mm});
            skArc(sketch, "E92.MirrorCS", {"start": v(-15.5, -120) * mm, "mid": v(-0.5, -135) * mm, "end": v(14.5, -120) * mm});
            skLineSegment(sketch, "E93.MirrorCS", {"start": v(-15.5, -108) * mm, "end": v(-15.5, -120) * mm});
            skLineSegment(sketch, "E94.MirrorCS", {"start": v(-33.5, -90) * mm, "end": v(-15.5, -108) * mm});
            skLineSegment(sketch, "E95.MirrorCS", {"start": v(-0.5, -120) * mm, "end": v(-0.5, -90) * mm, "construction": true});
            skCircle(sketch, "E96.MirrorC", {"center": v(-0.5, -120) * mm, "radius": 6 * mm});
            skSolve(sketch);
        }
        {
            var Q0;
            Q0=makeQuery(id+"F16.imprint","IMPRINT",FACE,{"disambiguationData":[TD([[makeQuery(id+"F16.imprint","IMPRINT",EDGE,{"derivedFrom":makeQuery(id+"F1.opExtrude","CAP_EDGE",EDGE,{"disambiguationData":[OSD([sQuery(id+"F0.wireOp",EDGE,"E1.bottom")])],"isStart":true})}),1.0]])]});
            var Q1;
            Q1=makeQuery(id+"F17.imprint","IMPRINT",FACE,{"disambiguationData":[TD([[makeQuery(id+"F17.imprint","IMPRINT",EDGE,{"derivedFrom":sQuery(id+"F17.wireOp",EDGE,"E82")}),-1.0]])]});
            var Q2;
            {var subQ0=sQuery(id+"F17.wireOp",EDGE,"E90.MirrorCS");Q2=makeQuery(id+"F17.imprint","IMPRINT",FACE,{"disambiguationData":[TD([[makeQuery(id+"F17.imprint","IMPRINT",EDGE,{"derivedFrom":subQ0}),-1.0]])]});}
            var Q3;
            Q3=makeQuery(id+"F2.opExtrude","CAP_FACE",FACE,{"disambiguationData":[OSD([sQuery(id+"F0.wireOp",EDGE,"E12"),sQuery(id+"F0.wireOp",EDGE,"E13"),sQuery(id+"F0.wireOp",EDGE,"E14"),sQuery(id+"F0.wireOp",EDGE,"E15"),sQuery(id+"F0.wireOp",EDGE,"E17.filletArc"),sQuery(id+"F0.wireOp",EDGE,"E18.filletArc"),sQuery(id+"F0.wireOp",EDGE,"E19.filletArc"),sQuery(id+"F0.wireOp",EDGE,"E20.filletArc"),sQuery(id+"F0.wireOp",EDGE,"E25.0"),sQuery(id+"F0.wireOp",EDGE,"E25.1"),sQuery(id+"F0.wireOp",EDGE,"E25.2"),sQuery(id+"F0.wireOp",EDGE,"E25.3"),sQuery(id+"F0.wireOp",EDGE,"E25.4"),sQuery(id+"F0.wireOp",EDGE,"E25.5"),sQuery(id+"F0.wireOp",EDGE,"E25.6"),sQuery(id+"F0.wireOp",EDGE,"E25.7")])],"isStart":false});
            extrude(context, id + "F18", {"entities" : qUnion([Q0, Q1, Q2]), "operationType" : NewBodyOperationType.ADD, "endBound" : BoundingType.UP_TO_SURFACE, "endBoundEntityFace" : qUnion([Q3]), "depth" : 25 * mm});
        }
    });
